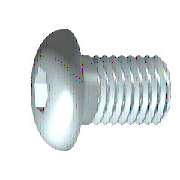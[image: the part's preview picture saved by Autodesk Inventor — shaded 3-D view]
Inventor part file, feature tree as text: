
AUTODESK INVENTOR PART (.ipt)
format: ipt  version: 2023.4 (Build 274418000, 418)  size: 201,216 bytes
history: native  units: mm (DEFAULTED — no unit token found)
features: extrude x1, plane x1, fillet x1
ambient origin geometry x7: Origin, YZ Plane, XY Plane, X Axis, Y Axis, Z Axis, Center Point
bodies: Solid1 (feature_tree), Body (feature_tree)
feature tree (3):
  extrude  "Slot"  Depth=4.2416mm
  plane  "Work Plane1"
  fillet  "Fillet2"  Radius=2.1083mm
